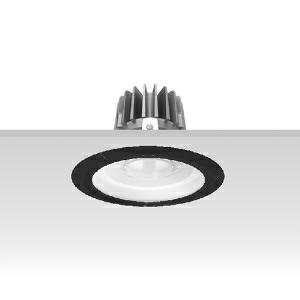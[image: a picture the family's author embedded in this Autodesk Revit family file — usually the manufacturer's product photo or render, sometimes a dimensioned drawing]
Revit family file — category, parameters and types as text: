
# Revit family: 3f_filippi_-_3f_reno_bianco_ampio_3f_filippi_-_30358_a01024_-_3f_reno_150_wh_2000-840_ep_wide___vt_bk_cf99
name_source: partatom
category: Lighting Fixtures
units: mm (PartAtom-declared; Revit-internal decimal feet)

## family parameters
Cut with Voids When Loaded = No
Host = Face
Light Source = No
Part Type = Normal
Room Calculation Point = No
Round Connector Dimension = Use Diameter
Shared = No

## types (1)
- 3F Filippi - 3F Reno Bianco Ampio (1 x LED, 1972 lm, 21 W, 4000 K)
    Apparent Load = 21 VA
    Approval mark = ENEC
    CIE Flux Codes = 74 93 99 100 100
    Color Rendering = 80
    Color Temperature = 4000 K
    Control Gear = Electronic ballast
    Default Elevation = 1800 mm
    Description = ILLUMINOTECHNICAL
Luminous efficiency 100% (DLOR 100%, ULOR 0%).
Initial luminous flux of the luminaire 1972 lm.
Emergency luminaire luminous flux BLF 20%.
Direct symmetric wide distribution.
Installation Interdistance Transv.D = 1.54 x hu - Long.D = 1.54 x hu.
Tabular UGR (CIE 117 - 4H-8H; S=0.25H; 70/50/20): RUG 23.3 - 23.2.
Beam angle: 74° - 73°.
Luminous efficacy 94 lm/W.
Lifetime (L90/B10): 30000 h. (tq+25°C)
Lifetime (L85/B10): 50000 h. (tq+25°C)
Lifetime (L70/B10): 80000 h. (tq+25°C)
Sudden decreased luminous flux after 50000 hours: 0% (C0).
Photobiological safety in compliance with IEC/TR 62778: RG0 risk exempt, (IEC 62471).
In compliance with IEC/EN 62722-2-1 - IEC/EN 62717 standards.

SOURCE
Compact LED module 2000/840.
Energy efficiency class (UE 2019/2020 - UE 2019/2015): D.
CIE 13.3 Colour rendering index: CRI >80 (R9 <50%).
IES TM-30 Fidelity Index: Rf = 84 Rg = 95.
CCT nominal colour temperature 4000 K.
Colour initial tolerance (MacAdam): SDCM 3.
Zhaga Book 3 compliant.

MECHANICAL
Passive heat dissipator in die-casting aluminium, oversized, for optimum thermal management of the LED module.
Parabolic element with graduated/concentric rings in white polycarbonate.
Transparent external lens with glossy and satin differentiated surfaces, with a cooling and anti-insect system in methacrylate (PMMA).
Fastening spring clips in stainless steel.
Dimensions: diameter 176 mm, height 111 mm. Weight 1.3 kg.
IP44 protection degree for exposed part, IP20 for recessed part.
Mechanical strength to impacts IK06 (1 joule).
Glow-wire test resistance 650°C.

ELECTRICAL
Wiring on a separate unit.
Halogen Free electronic wiring 230V-50/60Hz, power factor 0.90, THD <25%, constant output current, SELV, class II, 1 driver.
Power of the luminaire 21 W.
CE - IEC 60598-1 - EN 60598-1.
EP maintained emergency wiring on board, 1h duration, 24h recharge; compliant with EN 60598-2-22, excluding high risk areas.
SAFE FLICKER: PstLM=<1 and SVM=<0.4 (IEC TR 61547-1 and IEC TR 63158), to ensure a more comfortable and safe light.
Ambient temperature from +5°C to +25°C.
Temperature class T6 max 85°C.
Relative humidity UR: <85%.

INSTALLATION
Pull-up recessed fitting.
False ceiling carving: 150 mm.
All accessories dedicated to this product are available on the Catalog and on our website www.3F-Filippi.com.

ACCESSORIES
A01024 - VT transparent glass, tempered, not flammable, locked and in line with the trim, in black polycarbonate.

APPLICATIONS
Environments: architectural, commercial, exhibition areas, transit areas, corridors, shops, display windows, service areas.
In false ceilings with narrow voids.

WARNING
Luminaire designed for disposal/recycling at end-of-life.
Replaceable (LED only) light source by a professional. Replaceable control gear by a professional.
    Height = 0 mm  [stored 0 ft]
    Lamp = 1 x LED
    Lamp Light Flux = 1972 lm
    Lamp Power = 21 W
    Lamp count = 1
    Length = 176 mm
    Lifetime = 50000 h
    Luminous efficacy = 94 lm/W
    Manufacturer = 3F Filippi
    ModVariant = No
    Model = 3F Filippi - 30358+A01024 - 3F Reno 150 WH 2000-840 EP WIDE + VT BK
    Mounting Place = Ceiling
    Mounting Type = Recessed
    Number of Poles = 1
    OnlyDefault = Yes
    Power Factor = 1
    Product Name = 3F Filippi - 3F Reno Bianco Ampio
    Product group = recessed luminaire
    ProductGroupID = 4
    Protection Class = Protection class II
    Protection Degree = IP 20
    RLX_Detail_Level = 1
    RLX_Emergency_Light_Flux = 0 lm
    RLX_Emergency_Type = 0
    RLX_Emergency_Type_DB = No
    RlxData = <blob elided: 84941 chars, md5=e6563c4a>
    Socket = socket
    Standby Power = 0 W
    System Light Flux = 1972 lm
    System Power = 21 W
    Type Comments = Product without accessories
    Type Image = 3ffilippi_3f_reno_150_wh_d100__a01024.jpg
    URL = http://relux.com
    VarID = ---
    Voltage = 0 V
    Weight = 0.00 kg
    Width = 0 mm  [stored 0 ft]

note: [stored X ft] marks values corroborated as IEEE doubles in the binary element streams (Revit-internal decimal feet)

## geometry (parser evidence)
native form markers: Blend x4, Sweep x11
no freeform markers — native parametric forms only
